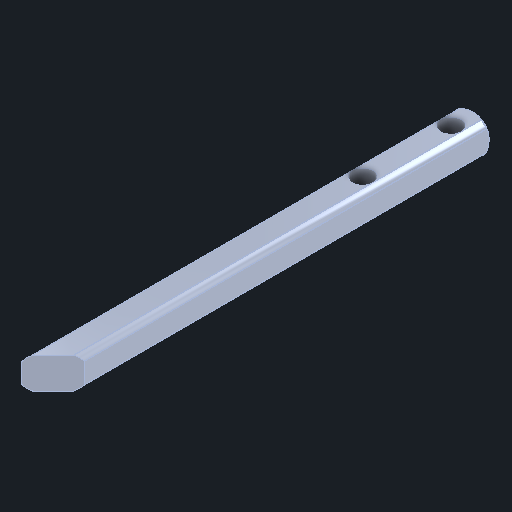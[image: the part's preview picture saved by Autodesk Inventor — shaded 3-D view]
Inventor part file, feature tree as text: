
AUTODESK INVENTOR PART (.ipt)
format: ipt  version: 2025 (Build 290162000, 162)  size: 209,920 bytes
history: native  units: in
note: dims shown in document units (in); Inventor stores cm internally (conversion verified against a paired STEP export)
features: other x50, extrude x4, sketch x4, thicken_offset x1
ambient origin geometry x8: Origin, YZ Plane, XZ Plane, XY Plane, X Axis, Y Axis, Z Axis, Center Point
bodies: Solid1 (feature_tree)
feature tree (59):
  other  "Table"
  other  "Shaft HS 0.5 in"
  other  "Shaft HS 1.0 in"
  other  "Shaft HS 1.5 in"
  other  "Shaft HS 2.0 in"
  other  "Shaft HS 2.5 in"
  other  "Shaft HS 3.0 in"
  other  "Shaft HS 3.5 in"
  other  "Shaft HS 4.0 in"
  other  "Shaft HS 4.5 in"
  other  "Shaft HS 5.0 in"
  other  "Shaft HS 5.5 in"
  other  "Shaft HS 6.0 in"
  other  "Shaft HS 6.5 in"
  other  "Shaft HS 7.0 in"
  other  "Shaft HS 7.5 in"
  other  "Shaft HS 8.0 in"
  other  "Shaft HS 8.5 in"
  other  "Shaft HS 9.0 in"
  other  "Shaft HS 9.5 in"
  other  "Shaft HS 10.0 in"
  other  "Shaft HS 10.5 in"
  other  "Shaft HS 11.0 in"
  other  "Shaft HS 11.5 in"
  other  "Shaft HS 12.0 in"
  other  "Shaft HS 12.5 in"
  other  "Shaft HS 13.0 in"
  other  "Shaft HS 13.5 in"
  other  "Shaft HS 14.0 in"
  other  "Shaft HS 14.5 in"
  other  "Shaft HS 15.0 in"
  other  "Shaft HS 15.5 in"
  other  "Shaft HS 16.0 in"
  other  "Shaft HS 16.5 in"
  other  "Shaft HS 17.0 in"
  other  "Shaft HS 17.5 in"
  other  "Shaft HS 18.0 in"
  other  "Shaft HS 18.5 in"
  other  "Shaft HS 19.0 in"
  other  "Shaft HS 19.5 in"
  other  "Shaft HS 20.0 in"
  other  "Shaft HS 20.5 in"
  other  "Shaft HS 21.0 in"
  other  "Shaft HS 21.5 in"
  other  "Shaft HS 22.0 in"
  other  "Shaft HS 22.5 in"
  other  "Shaft HS 23.0 in"
  other  "Shaft HS 23.5 in"
  other  "Shaft HS 24.0 in"
  extrude  "Extrusion1"  Depth=12.1875in
  thicken_offset  "Thicken1"
  extrude  "Extrusion2"  Depth=20.625in
  extrude  "Extrusion3"  Depth=0.165in
  extrude  "Extrusion4"  Depth=0.3084in
  sketch  "Sketch2"  dims[d0=0.0625in d1=0.0in d2=12.1875in]
  sketch  "Sketch3"  dims[d3=12.125in d4=20.625in]
  sketch  "Sketch4"  dims[d5=0.0in d6=0.165in]
  sketch  "Sketch5"  dims[d8=1.0in d9=0.0in d10=0.3084in d11=1.0in d12=0.0in d13=0.165in]
  other  "Cut-Revolve3"
